# Revit family: CC_SQ
name_source: partatom
category: Lighting Fixtures
units: mm (PartAtom-declared; Revit-internal decimal feet)

## family parameters
Cut with Voids When Loaded = No
Host = Face
Light Source = No
OmniClass Number = 23.80.70.11.21
OmniClass Title = Emergency Lighting
Part Type = Normal
Room Calculation Point = No
Round Connector Dimension = Use Diameter
Shared = No

## types (2) — shared parameters
Application = Stair-wells, hallways, offices and commercial applications
Certification = UL924 Listed for Damp Location
NFPA 101 and NFPA 70
OSHA
Default Elevation = 48.000"
Description = The white Exit housing and lamp-heads are made of high impact UL flame rated thermoplastic. The square LED lamp-heads are fully adjustable and glare-free. Snap together design for quick and easy installation with option of wall or ceiling mount. The CC SQ Series includes a high lumen output lamp-head run at 1.7 watts per lamp.
Double Face = No
Features = •	 LED life-cycle of more than 10 years
•	 Molded-in template for Quick installation
•	 Dual-voltage 120 or 277V AC input
•	 Includes long-life Nickel Cadmium battery for UL recognized
90 minute emergency lighting
•	 Damp Location Listed 20°C to 30°C (68°F to 86°F)
•	 Provided with test switch and AC-On indicator
•	 Lamp-heads are fully adjustable
•	 Canopy included
Finish = White
Glass = light Glass
Holder Material = Steel
Lamp = LED Lamp
Load Classification = Lighting
Manufacturer = Compass Products
Single Face = Yes
Type Comments = Exit Light
URL = https://www.currentlighting.com
Wall Plate Material = White
Warranty = 2 year full unit warranty

## per-type parameters (varying)
| type | Apparent Load | Lens | Wattage Comments | Watts |
| CCGHOSQ | 5 VA | Green Glass | 5.00 W | 5 W |
| CCRHOSQ | 4 VA | Red Glass | 3.90 W | 4 W |

note: column(s) folded — value = type name in every type: Model

## geometry (parser evidence)
native form markers: Blend x6, Sweep x5
no freeform markers — native parametric forms only
